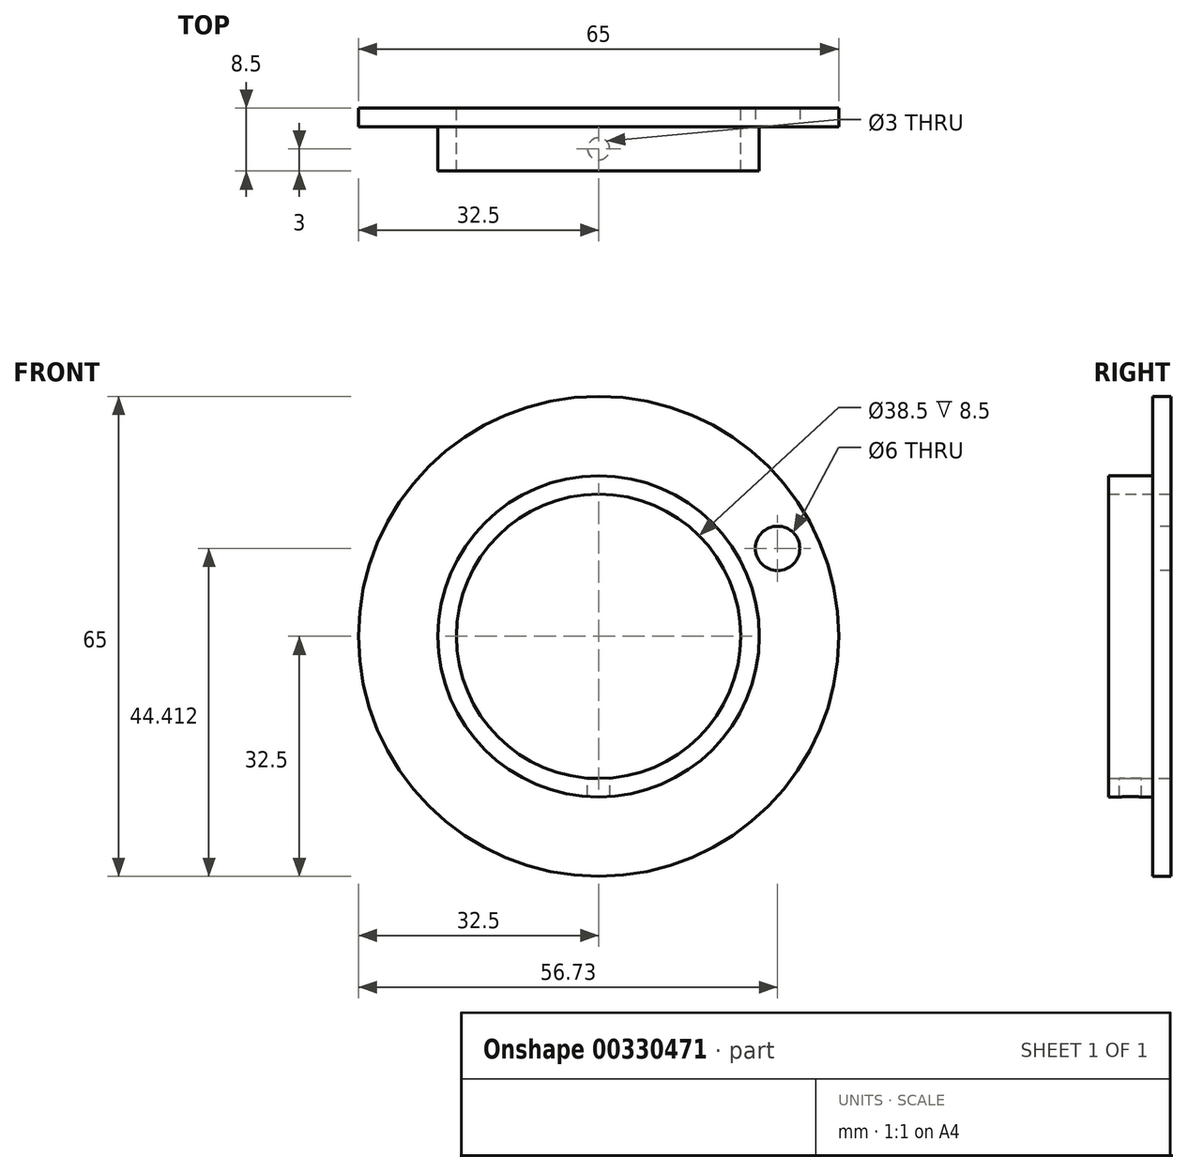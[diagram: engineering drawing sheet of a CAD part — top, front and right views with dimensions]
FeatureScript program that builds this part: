
annotation { "Feature Type Name" : "Feature", "Feature Type Description" : "" }
export const myFeature = defineFeature(function(context is Context, id is Id, definition is map)
    precondition{}
    {
        {
            var Q0;
            Q0=qCreatedBy(makeId("Front.planeOp"),FACE);
            var sketch = newSketch(context, id + "F0", { "sketchPlane" : qUnion([Q0])});
            skCircle(sketch, "E0", {"center": v(0, 0) * mm, "radius": 21.75 * mm});
            skCircle(sketch, "E1.0", {"center": v(0, 0) * mm, "radius": 19.25 * mm});
            skSolve(sketch);
        }
        {
            var Q0;
            Q0 = qSketchRegion(id + "F0", true);
            extrude(context, id + "F1", {"entities" : qUnion([Q0]), "depth" : 6 * mm});
        }
        {
            var Q0;
            Q0=qCreatedBy(makeId("Front.planeOp"),FACE);
            var sketch = newSketch(context, id + "F2", { "sketchPlane" : qUnion([Q0])});
            skCircle(sketch, "E2", {"center": v(0, 0) * mm, "radius": 32.5 * mm});
            skSolve(sketch);
        }
        {
            var Q0;
            Q0 = qSketchRegion(id + "F2", true);
            extrude(context, id + "F3", {"entities" : qUnion([Q0]), "operationType" : NewBodyOperationType.ADD, "oppositeDirection" : true, "depth" : 2.5 * mm});
        }
        {
            var Q0;
            Q0=qCreatedBy(makeId("Front.planeOp"),FACE);
            var sketch = newSketch(context, id + "F4", { "sketchPlane" : qUnion([Q0])});
            skCircle(sketch, "E3", {"center": v(0, 0) * mm, "radius": 19.25 * mm});
            skSolve(sketch);
        }
        {
            var Q0;
            Q0 = qSketchRegion(id + "F4", true);
            extrude(context, id + "F5", {"entities" : qUnion([Q0]), "operationType" : NewBodyOperationType.REMOVE, "oppositeDirection" : true, "depth" : 25 * mm});
        }
        {
            var Q0;
            Q0=qCreatedBy(makeId("Top.planeOp"),FACE);
            var sketch = newSketch(context, id + "F6", { "sketchPlane" : qUnion([Q0])});
            skCircle(sketch, "E4", {"center": v(0, -3) * mm, "radius": 1.5 * mm});
            skSolve(sketch);
        }
        {
            var Q0;
            Q0 = qSketchRegion(id + "F6", true);
            extrude(context, id + "F7", {"entities" : qUnion([Q0]), "operationType" : NewBodyOperationType.REMOVE, "oppositeDirection" : true, "depth" : 25 * mm});
        }
        {
            var Q0;
            {var subQ0=sQuery(id+"F2.wireOp",EDGE,"E2");Q0=makeQuery(id+"F3.boolean.opBoolean","SPLIT",FACE,{"disambiguationData":[TD([makeQuery(id+"F1.opExtrude","SWEPT_FACE",FACE,{"disambiguationData":[OSD([sQuery(id+"F0.wireOp",EDGE,"E0")])]})])],"derivedFrom":makeQuery(id+"F3.opExtrude","CAP_FACE",FACE,{"disambiguationData":[OSD([subQ0])],"isStart":true})});}
            var sketch = newSketch(context, id + "F8", { "sketchPlane" : qUnion([Q0])});
            skCircle(sketch, "E5", {"center": v(24.23, 11.91) * mm, "radius": 3 * mm});
            skSolve(sketch);
        }
        {
            var Q0;
            Q0 = qSketchRegion(id + "F8", true);
            extrude(context, id + "F9", {"entities" : qUnion([Q0]), "operationType" : NewBodyOperationType.REMOVE, "oppositeDirection" : true, "depth" : 25 * mm});
        }
    });
